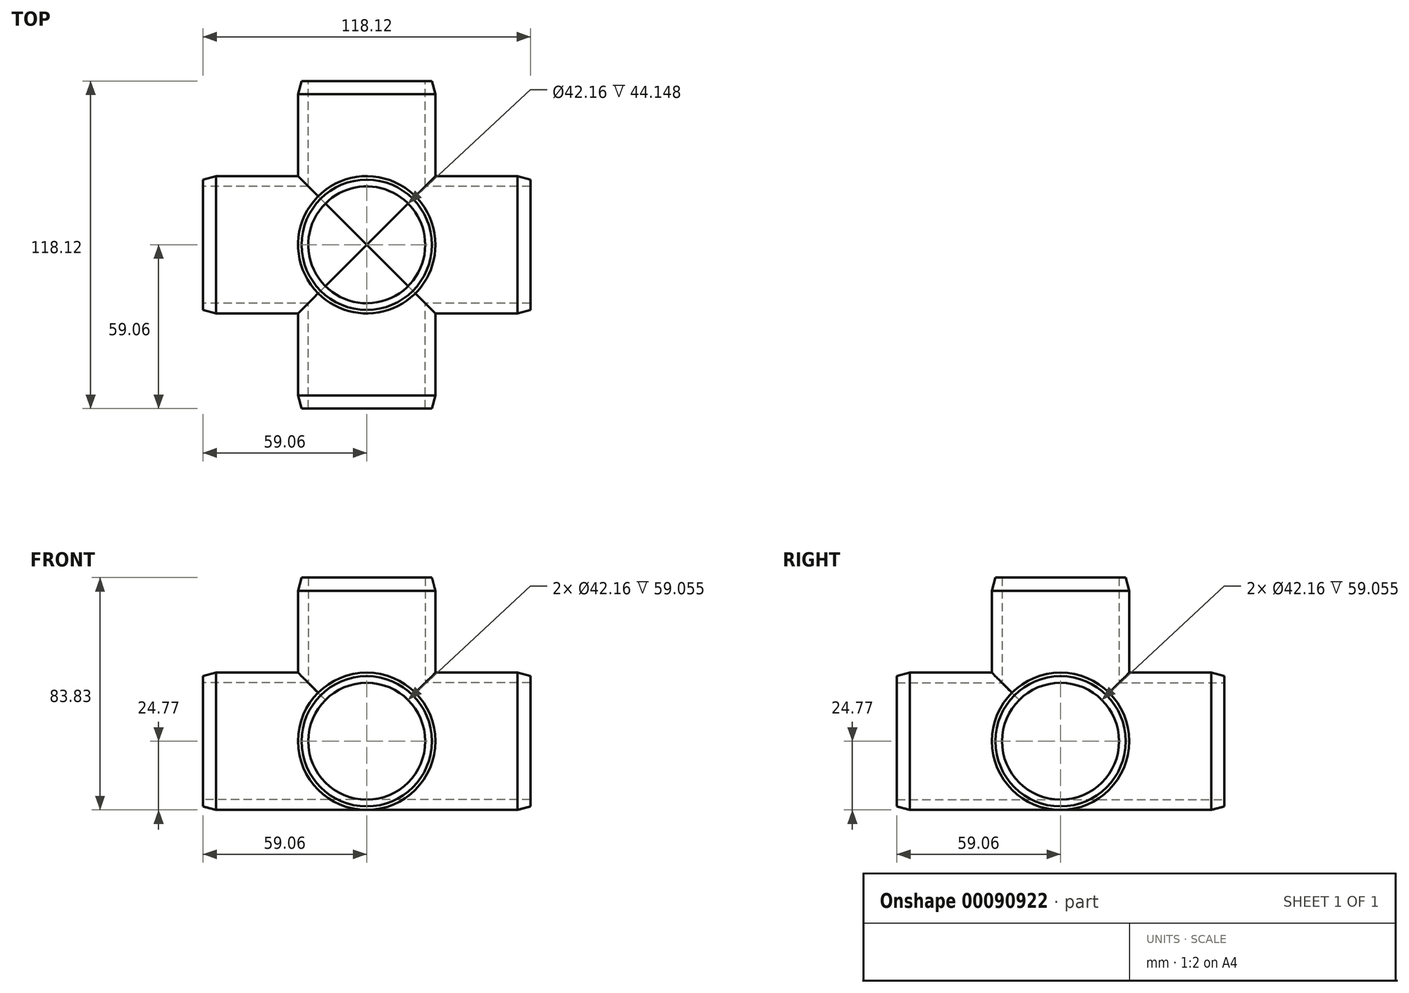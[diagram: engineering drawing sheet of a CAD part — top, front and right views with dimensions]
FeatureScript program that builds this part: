
annotation { "Feature Type Name" : "Feature", "Feature Type Description" : "" }
export const myFeature = defineFeature(function(context is Context, id is Id, definition is map)
    precondition{}
    {
        {
            var Q0;
            Q0=qCreatedBy(makeId("Front.planeOp"),FACE);
            var sketch = newSketch(context, id + "F0", { "sketchPlane" : qUnion([Q0])});
            skCircle(sketch, "E0", {"center": v(0, 0) * mm, "radius": 21.08 * mm});
            skCircle(sketch, "E1.0", {"center": v(0, 0) * mm, "radius": 24.77 * mm});
            skSolve(sketch);
        }
        {
            var Q0;
            Q0=qSketchRegion(id+"F0",true);
            extrude(context, id + "F1", {"entities" : qUnion([Q0]), "endBound" : BoundingType.SYMMETRIC, "depth" : 118.11 * mm});
        }
        {
            var Q0;
            Q0=qCreatedBy(makeId("Top.planeOp"),FACE);
            var sketch = newSketch(context, id + "F2", { "sketchPlane" : qUnion([Q0])});
            skCircle(sketch, "E2", {"center": v(0, 0) * mm, "radius": 21.08 * mm});
            skCircle(sketch, "E3.0", {"center": v(0, 0) * mm, "radius": 24.77 * mm});
            skSolve(sketch);
        }
        {
            var Q0;
            Q0=qSketchRegion(id+"F2",true);
            extrude(context, id + "F3", {"entities" : qUnion([Q0]), "operationType" : NewBodyOperationType.ADD, "depth" : 59.05 * mm});
        }
        {
            var Q0;
            Q0=qCreatedBy(makeId("Right.planeOp"),FACE);
            var sketch = newSketch(context, id + "F4", { "sketchPlane" : qUnion([Q0])});
            skCircle(sketch, "E4", {"center": v(0, 0) * mm, "radius": 21.08 * mm});
            skCircle(sketch, "E5.0", {"center": v(0, 0) * mm, "radius": 24.77 * mm});
            skSolve(sketch);
        }
        {
            var Q0;
            Q0=qSketchRegion(id+"F4",true);
            extrude(context, id + "F5", {"entities" : qUnion([Q0]), "operationType" : NewBodyOperationType.ADD, "endBound" : BoundingType.SYMMETRIC, "depth" : 118.11 * mm});
        }
        {
            var Q0;
            Q0=makeQuery(id+"F4.imprint","IMPRINT",FACE,{"disambiguationData":[TD([[makeQuery(id+"F4.imprint","IMPRINT",EDGE,{"derivedFrom":sQuery(id+"F4.wireOp",EDGE,"E4")}),1.0]])]});
            extrude(context, id + "F6", {"entities" : qUnion([Q0]), "operationType" : NewBodyOperationType.REMOVE, "endBound" : BoundingType.THROUGH_ALL, "depth" : 25.4 * mm, "hasSecondDirection" : true, "secondDirectionBound" : SecondDirectionBoundingType.THROUGH_ALL, "secondDirectionOppositeDirection" : true, "secondDirectionDepth" : 25.4 * mm});
        }
        {
            var Q0;
            Q0=makeQuery(id+"F2.imprint","IMPRINT",FACE,{"disambiguationData":[TD([[makeQuery(id+"F2.imprint","IMPRINT",EDGE,{"derivedFrom":sQuery(id+"F2.wireOp",EDGE,"E2")}),1.0]])]});
            extrude(context, id + "F7", {"entities" : qUnion([Q0]), "operationType" : NewBodyOperationType.REMOVE, "endBound" : BoundingType.THROUGH_ALL, "depth" : 25.4 * mm});
        }
        {
            var Q0;
            Q0=makeQuery(id+"F0.imprint","IMPRINT",FACE,{"disambiguationData":[TD([[makeQuery(id+"F0.imprint","IMPRINT",EDGE,{"derivedFrom":sQuery(id+"F0.wireOp",EDGE,"E0")}),1.0]])]});
            extrude(context, id + "F8", {"entities" : qUnion([Q0]), "operationType" : NewBodyOperationType.REMOVE, "endBound" : BoundingType.THROUGH_ALL, "depth" : 25.4 * mm, "hasSecondDirection" : true, "secondDirectionBound" : SecondDirectionBoundingType.THROUGH_ALL, "secondDirectionOppositeDirection" : true, "secondDirectionDepth" : 25.4 * mm});
        }
        {
            var Q0;
            Q0=makeQuery(id+"F3.opExtrude","CAP_EDGE",EDGE,{"disambiguationData":[OSD([sQuery(id+"F2.wireOp",EDGE,"E3.0")])],"isStart":false});
            var Q1;
            Q1=makeQuery(id+"F1.opExtrude","CAP_EDGE",EDGE,{"disambiguationData":[OSD([sQuery(id+"F0.wireOp",EDGE,"E1.0")])],"isStart":false});
            var Q2;
            Q2=makeQuery(id+"F5.opExtrude","CAP_EDGE",EDGE,{"disambiguationData":[OSD([sQuery(id+"F4.wireOp",EDGE,"E5.0")])],"isStart":false});
            chamfer(context, id + "F9", {"entities" : qUnion([Q0, Q1, Q2]), "chamferType" : ChamferType.OFFSET_ANGLE, "width" : 1.27 * mm, "oppositeDirection" : false, "angle" : 75 * degree, "tangentPropagation" : true});
        }
        {
            var Q0;
            Q0=makeQuery(id+"F1.opExtrude","CAP_EDGE",EDGE,{"disambiguationData":[OSD([sQuery(id+"F0.wireOp",EDGE,"E1.0")])],"isStart":true});
            var Q1;
            Q1=makeQuery(id+"F5.opExtrude","CAP_EDGE",EDGE,{"disambiguationData":[OSD([sQuery(id+"F4.wireOp",EDGE,"E5.0")])],"isStart":true});
            chamfer(context, id + "F10", {"entities" : qUnion([Q0, Q1]), "chamferType" : ChamferType.OFFSET_ANGLE, "width" : 1.27 * mm, "oppositeDirection" : true, "angle" : 75 * degree, "tangentPropagation" : true});
        }
    });
